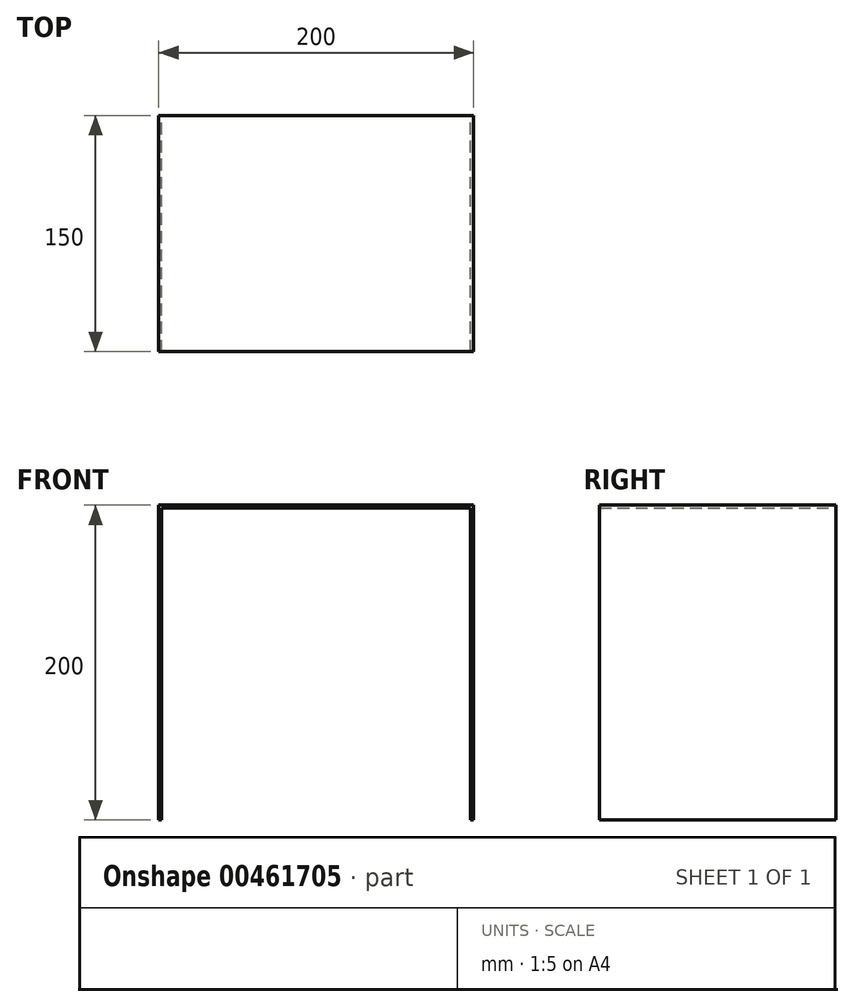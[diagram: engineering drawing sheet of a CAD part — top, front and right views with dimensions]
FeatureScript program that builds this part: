
annotation { "Feature Type Name" : "Feature", "Feature Type Description" : "" }
export const myFeature = defineFeature(function(context is Context, id is Id, definition is map)
    precondition{}
    {
        {
            var Q0;
            Q0=qCreatedBy(makeId("Front.planeOp"),FACE);
            var sketch = newSketch(context, id + "F0", { "sketchPlane" : qUnion([Q0])});
            skLineSegment(sketch, "E0.bottom", {"start": v(100, 100) * mm, "end": v(-100, 100) * mm});
            skLineSegment(sketch, "E0.left", {"start": v(100, 100) * mm, "end": v(100, -100) * mm});
            skLineSegment(sketch, "E0.right", {"start": v(-100, 100) * mm, "end": v(-100, -100) * mm});
            skPoint(sketch, "E0.middle", {"position": v(0, 0) * mm});
            skLineSegment(sketch, "E1.bottom", {"start": v(98.1, 98.1) * mm, "end": v(-98.1, 98.1) * mm});
            skLineSegment(sketch, "E1.left", {"start": v(98.1, 98.1) * mm, "end": v(98.1, -98.1) * mm});
            skLineSegment(sketch, "E1.right", {"start": v(-98.1, 98.1) * mm, "end": v(-98.1, -98.1) * mm});
            skLineSegment(sketch, "E2", {"start": v(-100, -100) * mm, "end": v(-98.1, -100) * mm});
            skLineSegment(sketch, "E3", {"start": v(100, -100) * mm, "end": v(98.1, -100) * mm});
            skLineSegment(sketch, "E4", {"start": v(98.1, -100) * mm, "end": v(98.1, -98.1) * mm});
            skLineSegment(sketch, "E5", {"start": v(-98.1, -100) * mm, "end": v(-98.1, -98.1) * mm});
            skSolve(sketch);
        }
        {
            var Q0;
            Q0=makeQuery(id+"F0.imprint","IMPRINT",FACE,{"disambiguationData":[TD([[makeQuery(id+"F0.imprint","IMPRINT",EDGE,{"derivedFrom":sQuery(id+"F0.wireOp",EDGE,"E0.bottom")}),1.0]])]});
            extrude(context, id + "F1", {"entities" : qUnion([Q0]), "depth" : 150 * mm});
        }
    });
